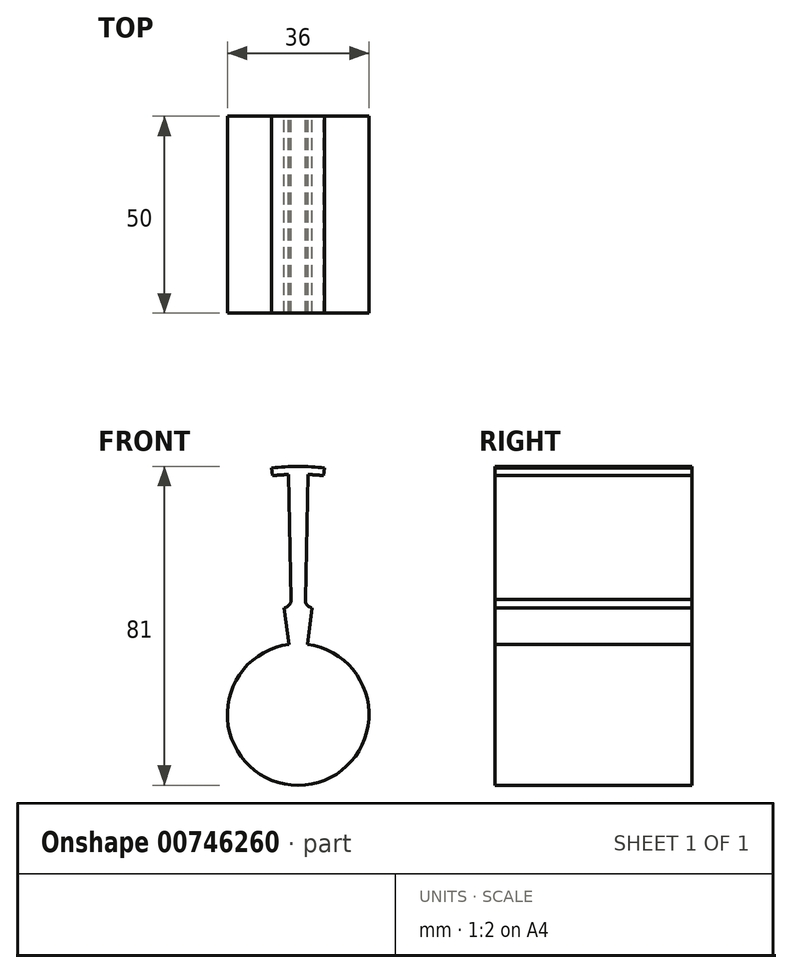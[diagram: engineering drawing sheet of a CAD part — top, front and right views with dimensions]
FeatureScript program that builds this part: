
annotation { "Feature Type Name" : "Feature", "Feature Type Description" : "" }
export const myFeature = defineFeature(function(context is Context, id is Id, definition is map)
    precondition{}
    {
        {
            var Q0;
            Q0=qCreatedBy(makeId("Front.planeOp"),FACE);
            var sketch = newSketch(context, id + "F0", { "sketchPlane" : qUnion([Q0])});
            skArc(sketch, "E0.MirrorC", {"start": v(-1.85, 29.2) * mm, "mid": v(-2.27, 27.78) * mm, "end": v(-3.56, 27.05) * mm});
            skLineSegment(sketch, "E1", {"start": v(-2.49, 60.97) * mm, "end": v(-1.85, 29.2) * mm});
            skLineSegment(sketch, "E2", {"start": v(2.48, 60.97) * mm, "end": v(1.84, 29.2) * mm});
            skLineSegment(sketch, "E3.MirrorCS", {"start": v(-6.75, 62.64) * mm, "end": v(-6.49, 60.67) * mm});
            skLineSegment(sketch, "E4.MirrorCS", {"start": v(6.75, 62.64) * mm, "end": v(6.49, 60.67) * mm});
            skArc(sketch, "E5.trimOffspring", {"start": v(6.75, 62.64) * mm, "mid": v(0, 63) * mm, "end": v(-6.75, 62.64) * mm});
            skArc(sketch, "E6.trimOffspring", {"start": v(6.49, 60.67) * mm, "mid": v(4.49, 60.85) * mm, "end": v(2.48, 60.97) * mm});
            skArc(sketch, "E7.trimOffspring", {"start": v(-2.49, 60.97) * mm, "mid": v(-4.49, 60.85) * mm, "end": v(-6.49, 60.67) * mm});
            skLineSegment(sketch, "E8", {"start": v(3.56, 27.05) * mm, "end": v(0, 0) * mm});
            skLineSegment(sketch, "E9", {"start": v(-3.56, 27.05) * mm, "end": v(0, 0) * mm});
            skLineSegment(sketch, "E10", {"start": v(1.84, 29.2) * mm, "end": v(1.85, 29.2) * mm});
            skArc(sketch, "E11", {"start": v(3.56, 27.05) * mm, "mid": v(2.27, 27.78) * mm, "end": v(1.85, 29.2) * mm});
            skCircle(sketch, "E12", {"center": v(0, 0) * mm, "radius": 18 * mm});
            skPoint(sketch, "E13.startSnap0", {"position": v(0, 63) * mm});
            skSolve(sketch);
        }
        {
            var Q0;
            Q0=qSketchRegion(id+"F0",true);
            extrude(context, id + "F1", {"entities" : qUnion([Q0]), "depth" : 50 * mm, "offsetDistance" : 25 * mm});
        }
        {
            var Q0;
            Q0 = qSketchRegion(id + "F0", true);
            extrude(context, id + "F2", {"entities" : qUnion([Q0]), "operationType" : NewBodyOperationType.ADD, "depth" : 25 * mm, "offsetDistance" : 25 * mm});
        }
    });
